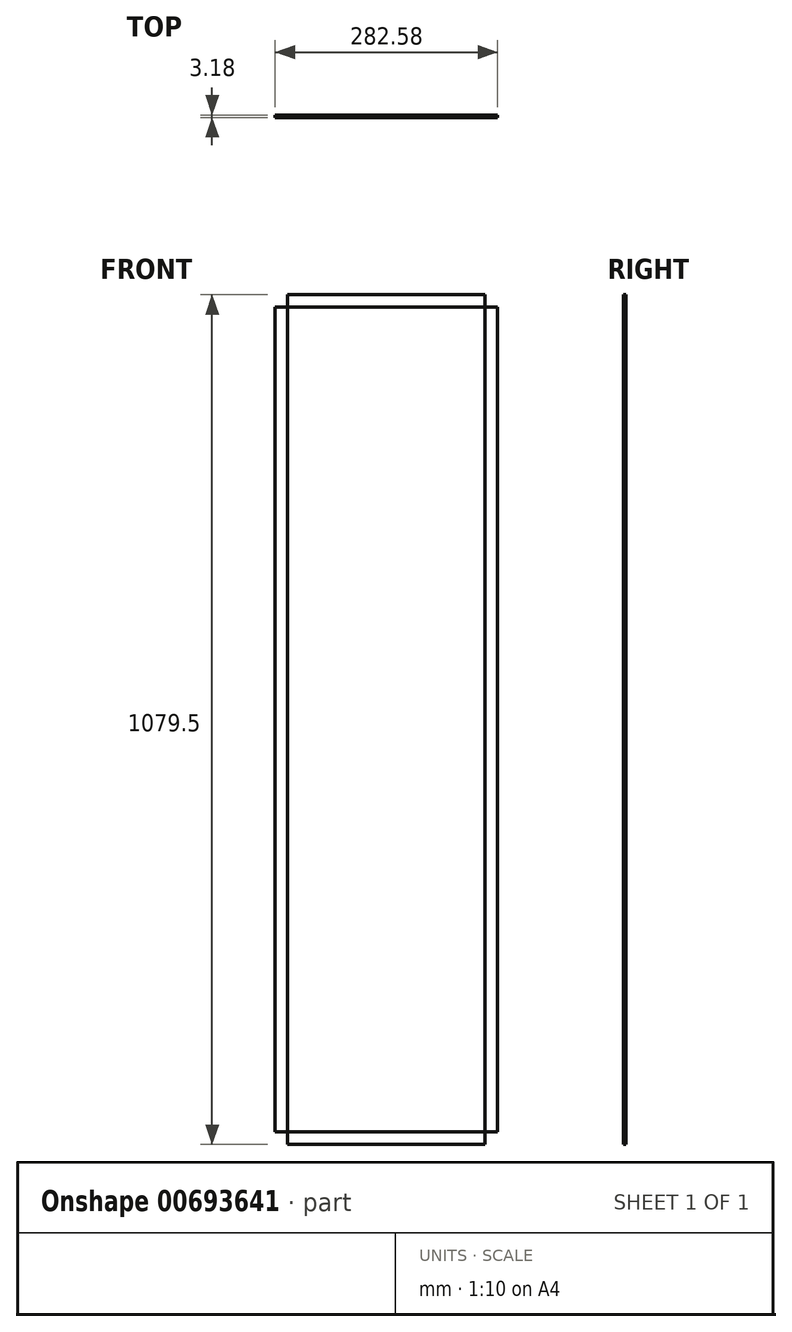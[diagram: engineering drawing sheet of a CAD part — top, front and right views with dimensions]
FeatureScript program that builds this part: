
annotation { "Feature Type Name" : "Feature", "Feature Type Description" : "" }
export const myFeature = defineFeature(function(context is Context, id is Id, definition is map)
    precondition{}
    {
        {
            var Q0;
            Q0=qCreatedBy(makeId("Front.planeOp"),FACE);
            var sketch = newSketch(context, id + "F0", { "sketchPlane" : qUnion([Q0])});
            skLineSegment(sketch, "E0.bottom", {"start": v(-4.6, 1031.02) * mm, "end": v(246.23, 1031.02) * mm});
            skLineSegment(sketch, "E0.top", {"start": v(-4.6, -16.73) * mm, "end": v(246.23, -16.73) * mm});
            skLineSegment(sketch, "E0.left", {"start": v(-4.6, 1031.02) * mm, "end": v(-4.6, -16.73) * mm});
            skLineSegment(sketch, "E0.right", {"start": v(246.23, 1031.02) * mm, "end": v(246.23, -16.73) * mm});
            skSolve(sketch);
        }
        {
            var Q0;
            Q0=makeQuery(id+"F0.imprint","IMPRINT",FACE,{"disambiguationData":[TD([[makeQuery(id+"F0.imprint","IMPRINT",EDGE,{"derivedFrom":sQuery(id+"F0.wireOp",EDGE,"E0.bottom")}),-1.0]])]});
            extrude(context, id + "F1", {"entities" : qUnion([Q0]), "endBound" : BoundingType.SYMMETRIC, "depth" : 3.17 * mm, "offsetDistance" : 25 * mm});
        }
        {
            var Q0;
            Q0=makeQuery(id+"F1.opExtrude","SWEPT_FACE",FACE,{"disambiguationData":[OSD([sQuery(id+"F0.wireOp",EDGE,"E0.right")])]});
            var sketch = newSketch(context, id + "F2", { "sketchPlane" : qUnion([Q0])});
            skLineSegment(sketch, "E1", {"start": v(1.59, 1031.02) * mm, "end": v(-1.59, 1031.02) * mm});
            skLineSegment(sketch, "E2", {"start": v(-1.59, 1031.02) * mm, "end": v(-1.59, -16.73) * mm});
            skLineSegment(sketch, "E3", {"start": v(-1.59, -16.73) * mm, "end": v(1.59, -16.73) * mm});
            skLineSegment(sketch, "E4", {"start": v(1.59, -16.73) * mm, "end": v(1.59, 1031.02) * mm});
            skSolve(sketch);
        }
        {
            var Q0;
            Q0 = qSketchRegion(id + "F2", true);
            extrude(context, id + "F3", {"entities" : qUnion([Q0]), "depth" : 15.88 * mm, "offsetDistance" : 25.4 * mm});
        }
        {
            var Q0;
            Q0=makeQuery(id+"F1.opExtrude","SWEPT_FACE",FACE,{"disambiguationData":[OSD([sQuery(id+"F0.wireOp",EDGE,"E0.bottom")])]});
            extrude(context, id + "F4", {"entities" : qUnion([Q0]), "depth" : 15.88 * mm, "offsetDistance" : 25.4 * mm});
        }
        {
            var Q0;
            Q0=makeQuery(id+"F1.opExtrude","SWEPT_FACE",FACE,{"disambiguationData":[OSD([sQuery(id+"F0.wireOp",EDGE,"E0.left")])]});
            extrude(context, id + "F5", {"entities" : qUnion([Q0]), "depth" : 15.88 * mm, "offsetDistance" : 25.4 * mm});
        }
        {
            var Q0;
            Q0=makeQuery(id+"F1.opExtrude","SWEPT_FACE",FACE,{"disambiguationData":[OSD([sQuery(id+"F0.wireOp",EDGE,"E0.top")])]});
            extrude(context, id + "F6", {"entities" : qUnion([Q0]), "depth" : 15.88 * mm, "offsetDistance" : 25.4 * mm});
        }
    });
